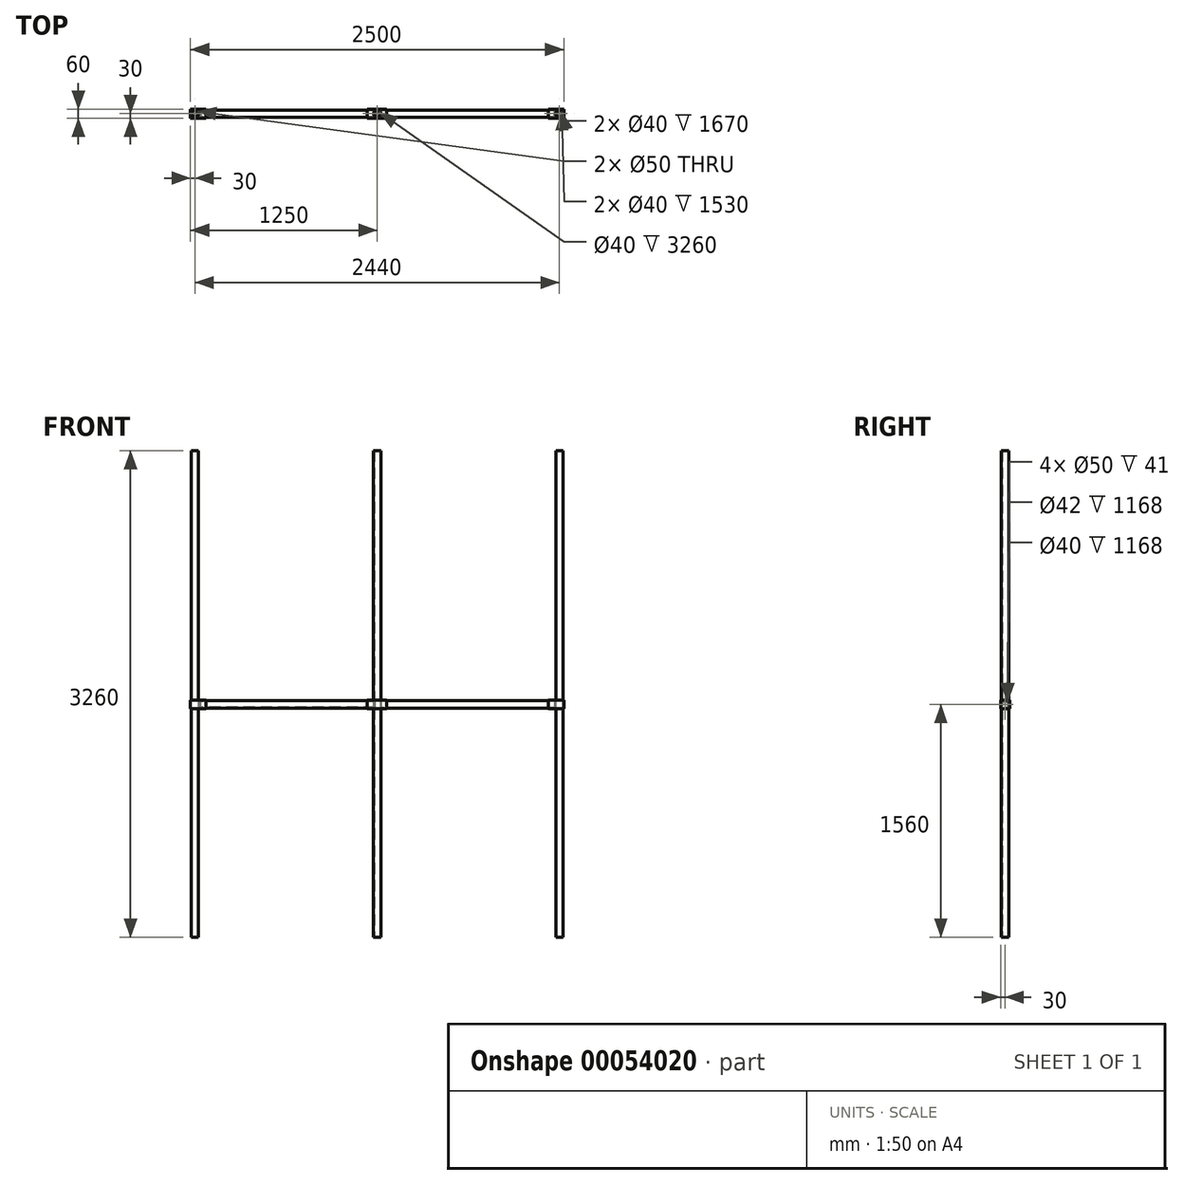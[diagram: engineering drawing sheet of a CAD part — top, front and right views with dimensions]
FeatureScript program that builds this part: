
annotation { "Feature Type Name" : "Feature", "Feature Type Description" : "" }
export const myFeature = defineFeature(function(context is Context, id is Id, definition is map)
    precondition{}
    {
        {
            var Q0;
            Q0=qCreatedBy(makeId("Top.planeOp"),FACE);
            var sketch = newSketch(context, id + "F0", { "sketchPlane" : qUnion([Q0])});
            skCircle(sketch, "E0", {"center": v(0, 0) * mm, "radius": 24 * mm});
            skCircle(sketch, "E1.0", {"center": v(0, 0) * mm, "radius": 20 * mm});
            skLineSegment(sketch, "E2", {"start": v(-610, 375.93) * mm, "end": v(-610, -600.88) * mm, "construction": true});
            skCircle(sketch, "E3.MirrorC", {"center": v(-1220, 0) * mm, "radius": 24 * mm});
            skCircle(sketch, "E4.MirrorC", {"center": v(-1220, 0) * mm, "radius": 20 * mm});
            skLineSegment(sketch, "E5", {"start": v(610, 336.85) * mm, "end": v(610, -639.97) * mm, "construction": true});
            skLineSegment(sketch, "E6", {"start": v(0, 384.05) * mm, "end": v(0, -643.9) * mm, "construction": true});
            skCircle(sketch, "E7.MirrorC", {"center": v(1220, 0) * mm, "radius": 24 * mm});
            skCircle(sketch, "E8.MirrorC", {"center": v(1220, 0) * mm, "radius": 20 * mm});
            skSolve(sketch);
        }
        {
            var Q0;
            Q0 = qSketchRegion(id + "F0", true);
            extrude(context, id + "F1", {"entities" : qUnion([Q0]), "depth" : 3260 * mm});
        }
        {
            var Q0;
            Q0=qCreatedBy(makeId("Front.planeOp"),FACE);
            var sketch = newSketch(context, id + "F2", { "sketchPlane" : qUnion([Q0])});
            skLineSegment(sketch, "E9", {"start": v(-2136.33, 1560) * mm, "end": v(2102.12, 1560) * mm, "construction": true});
            skLineSegment(sketch, "E10.rect.bottom", {"start": v(65, 1530) * mm, "end": v(-65, 1530) * mm});
            skLineSegment(sketch, "E10.rect.top", {"start": v(65, 1590) * mm, "end": v(-65, 1590) * mm});
            skLineSegment(sketch, "E10.rect.left", {"start": v(65, 1530) * mm, "end": v(65, 1590) * mm});
            skLineSegment(sketch, "E10.rect.right", {"start": v(-65, 1530) * mm, "end": v(-65, 1590) * mm});
            skPoint(sketch, "E10.rect.middle", {"position": v(0, 1560) * mm});
            skLineSegment(sketch, "E11.bottom", {"start": v(-1250, 1590) * mm, "end": v(-1145, 1590) * mm});
            skLineSegment(sketch, "E11.top", {"start": v(-1250, 1530) * mm, "end": v(-1145, 1530) * mm});
            skLineSegment(sketch, "E11.left", {"start": v(-1250, 1590) * mm, "end": v(-1250, 1530) * mm});
            skLineSegment(sketch, "E11.right", {"start": v(-1145, 1590) * mm, "end": v(-1145, 1530) * mm});
            skLineSegment(sketch, "E12", {"start": v(-1220, 0) * mm, "end": v(-1220, 713.03) * mm, "construction": true});
            skLineSegment(sketch, "E13", {"start": v(-1220, 713.03) * mm, "end": v(-1220, 2527.16) * mm, "construction": true});
            skLineSegment(sketch, "E14", {"start": v(-1220, 2527.16) * mm, "end": v(-1220, 3194.12) * mm, "construction": true});
            skLineSegment(sketch, "E15", {"start": v(-1220, 3194.12) * mm, "end": v(-1220, 3345.25) * mm, "construction": true});
            skLineSegment(sketch, "E16", {"start": v(0, 1560) * mm, "end": v(0, -308.11) * mm, "construction": true});
            skLineSegment(sketch, "E17", {"start": v(0, 1560) * mm, "end": v(0, 3349.8) * mm, "construction": true});
            skLineSegment(sketch, "E18.MirrorCS", {"start": v(1220, 0) * mm, "end": v(1220, 713.03) * mm, "construction": true});
            skLineSegment(sketch, "E19.MirrorCS", {"start": v(1220, 713.03) * mm, "end": v(1220, 2527.16) * mm, "construction": true});
            skLineSegment(sketch, "E20.MirrorCS", {"start": v(1220, 2527.16) * mm, "end": v(1220, 3194.12) * mm, "construction": true});
            skLineSegment(sketch, "E21.MirrorCS", {"start": v(1250, 1590) * mm, "end": v(1145, 1590) * mm});
            skLineSegment(sketch, "E22.MirrorCS", {"start": v(1250, 1530) * mm, "end": v(1145, 1530) * mm});
            skLineSegment(sketch, "E23.MirrorCS", {"start": v(1145, 1590) * mm, "end": v(1145, 1530) * mm});
            skLineSegment(sketch, "E24.MirrorCS", {"start": v(1250, 1590) * mm, "end": v(1250, 1530) * mm});
            skSolve(sketch);
        }
        {
            var Q0;
            Q0 = qSketchRegion(id + "F2", true);
            extrude(context, id + "F3", {"entities" : qUnion([Q0]), "depth" : 30 * mm, "hasSecondDirection" : true, "secondDirectionOppositeDirection" : true, "secondDirectionDepth" : 30 * mm});
        }
        {
            var Q0;
            Q0=makeQuery(id+"F3.opExtrude","SWEPT_FACE",FACE,{"disambiguationData":[OSD([sQuery(id+"F2.wireOp",EDGE,"E11.bottom")])]});
            var sketch = newSketch(context, id + "F4", { "sketchPlane" : qUnion([Q0])});
            skLineSegment(sketch, "E25", {"start": v(-1220, 42.42) * mm, "end": v(-1220, -45.65) * mm, "construction": true});
            skCircle(sketch, "E26", {"center": v(-1220, 0) * mm, "radius": 25 * mm});
            skCircle(sketch, "E27.MirrorC", {"center": v(1220, 0) * mm, "radius": 25 * mm});
            skSolve(sketch);
        }
        {
            var Q0;
            Q0 = qSketchRegion(id + "F4", true);
            extrude(context, id + "F5", {"entities" : qUnion([Q0]), "operationType" : NewBodyOperationType.REMOVE, "oppositeDirection" : true, "depth" : 60 * mm});
        }
        {
            var Q0;
            Q0=makeQuery(id+"F3.opExtrude","SWEPT_FACE",FACE,{"disambiguationData":[OSD([sQuery(id+"F2.wireOp",EDGE,"E11.right")])]});
            var sketch = newSketch(context, id + "F6", { "sketchPlane" : qUnion([Q0])});
            skCircle(sketch, "E28", {"center": v(0, 1560) * mm, "radius": 25 * mm});
            skPoint(sketch, "E28.centerSnap0", {"position": v(0, 1530) * mm});
            skPoint(sketch, "E28.centerSnap1", {"position": v(-30, 1560) * mm});
            skSolve(sketch);
        }
        {
            var Q0;
            Q0=makeQuery(id+"F3.opExtrude","SWEPT_FACE",FACE,{"disambiguationData":[OSD([sQuery(id+"F2.wireOp",EDGE,"E10.rect.right")])]});
            var sketch = newSketch(context, id + "F7", { "sketchPlane" : qUnion([Q0])});
            skCircle(sketch, "E29", {"center": v(0, 1560) * mm, "radius": 25 * mm});
            skPoint(sketch, "E29.centerSnap0", {"position": v(30, 1560) * mm});
            skPoint(sketch, "E29.centerSnap1", {"position": v(0, 1590) * mm});
            skSolve(sketch);
        }
        {
            var Q0;
            Q0=makeQuery(id+"F3.opExtrude","SWEPT_FACE",FACE,{"disambiguationData":[OSD([sQuery(id+"F2.wireOp",EDGE,"E23.MirrorCS")])]});
            var sketch = newSketch(context, id + "F8", { "sketchPlane" : qUnion([Q0])});
            skCircle(sketch, "E30", {"center": v(0, 1560) * mm, "radius": 25 * mm});
            skPoint(sketch, "E30.centerSnap0", {"position": v(0, 1590) * mm});
            skPoint(sketch, "E30.centerSnap1", {"position": v(30, 1560) * mm});
            skSolve(sketch);
        }
        {
            var Q0;
            Q0=makeQuery(id+"F3.opExtrude","SWEPT_FACE",FACE,{"disambiguationData":[OSD([sQuery(id+"F2.wireOp",EDGE,"E10.rect.left")])]});
            var sketch = newSketch(context, id + "F9", { "sketchPlane" : qUnion([Q0])});
            skPoint(sketch, "E31", {"position": v(0, 1560) * mm});
            skPoint(sketch, "E31.positionSnap0", {"position": v(0, 1590) * mm});
            skPoint(sketch, "E31.positionSnap1", {"position": v(-30, 1560) * mm});
            skCircle(sketch, "E32", {"center": v(0, 1560) * mm, "radius": 25 * mm});
            skSolve(sketch);
        }
        {
            var Q0;
            Q0 = qSketchRegion(id + "F9", true);
            extrude(context, id + "F10", {"entities" : qUnion([Q0]), "operationType" : NewBodyOperationType.REMOVE, "oppositeDirection" : true, "depth" : 41 * mm});
        }
        {
            var Q0;
            Q0 = qSketchRegion(id + "F8", true);
            extrude(context, id + "F11", {"entities" : qUnion([Q0]), "operationType" : NewBodyOperationType.REMOVE, "oppositeDirection" : true, "depth" : 41 * mm});
        }
        {
            var Q0;
            Q0 = qSketchRegion(id + "F7", true);
            extrude(context, id + "F12", {"entities" : qUnion([Q0]), "operationType" : NewBodyOperationType.REMOVE, "oppositeDirection" : true, "depth" : 41 * mm});
        }
        {
            var Q0;
            Q0 = qSketchRegion(id + "F6", true);
            extrude(context, id + "F13", {"entities" : qUnion([Q0]), "operationType" : NewBodyOperationType.REMOVE, "oppositeDirection" : true, "depth" : 41 * mm});
        }
        {
            var Q0;
            Q0=makeQuery(id+"F13.boolean.opBoolean","COPY",FACE,{"derivedFrom":makeQuery(id+"F13.opExtrude","CAP_FACE",FACE,{"disambiguationData":[OSD([sQuery(id+"F6.wireOp",EDGE,"E28")])],"isStart":false})});
            var sketch = newSketch(context, id + "F14", { "sketchPlane" : qUnion([Q0])});
            skCircle(sketch, "E33", {"center": v(0, 1560) * mm, "radius": 24 * mm});
            skSolve(sketch);
        }
        {
            var Q0;
            Q0 = qSketchRegion(id + "F14", true);
            extrude(context, id + "F15", {"entities" : qUnion([Q0]), "depth" : 1172 * mm});
        }
        {
            var Q0;
            Q0=makeQuery(id+"F10.boolean.opBoolean","COPY",FACE,{"derivedFrom":makeQuery(id+"F10.opExtrude","CAP_FACE",FACE,{"disambiguationData":[OSD([sQuery(id+"F9.wireOp",EDGE,"E32")])],"isStart":false})});
            extrude(context, id + "F16", {"entities" : qUnion([Q0]), "depth" : 1172 * mm});
        }
        {
            var Q0;
            Q0=makeQuery(id+"F15.opExtrude","CAP_FACE",FACE,{"disambiguationData":[OSD([sQuery(id+"F14.wireOp",EDGE,"E33")])],"isStart":false});
            shell(context, id + "F17", {"entities" : qUnion([Q0]), "thickness" : 4 * mm});
        }
        {
            var Q0;
            Q0=makeQuery(id+"F16.opExtrude","CAP_FACE",FACE,{"disambiguationData":[OSD([sQuery(id+"F9.wireOp",EDGE,"E32")])],"isStart":false});
            shell(context, id + "F18", {"entities" : qUnion([Q0]), "thickness" : 4 * mm});
        }
    });
